# Revit family: FU_Stool_Sandler_Cuba 4-1
name_source: partatom
category: Furniture
units: mm (PartAtom-declared; Revit-internal decimal feet)

## family parameters
Always vertical = Yes
Cut with Voids When Loaded = No
OmniClass Number = 23.40.20.00
OmniClass Title = General Furniture and Specialties
Room Calculation Point = No
Shared = No
Work Plane-Based = No

## types (1)
- Cuba 4.1
    Default Elevation = 0 mm  [stored 0 ft]
    Depth = 460 mm  [stored 1.50919 ft]
    Description = Polypropylene counter stool on a four leg steel frame.
    Frame = Metal - Paint -AL VR - Capri Blue
    Height = 860 mm
    Manufacturer = Sandler
    Model = Cuba 4.1
    Polypropylene = Metal - Paint -AL VR - Water Blue
    URL = https://www.sandlerseating.com
    Width = 510 mm  [stored 1.67323 ft]

note: [stored X ft] marks values corroborated as IEEE doubles in the binary element streams (Revit-internal decimal feet)

## geometry (parser evidence)
native form markers: Sweep x6
no freeform markers — native parametric forms only
